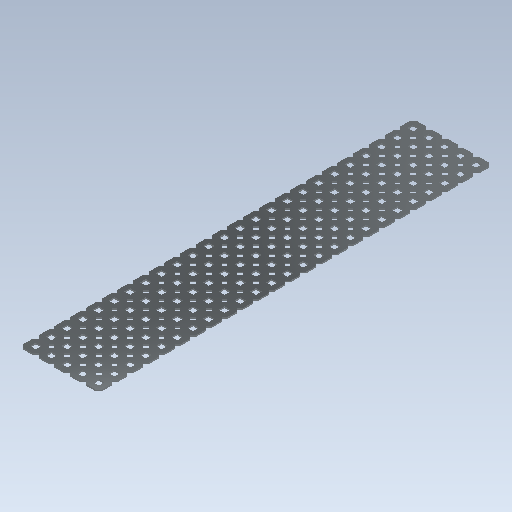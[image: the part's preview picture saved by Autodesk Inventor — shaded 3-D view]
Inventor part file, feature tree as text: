
AUTODESK INVENTOR PART (.ipt)
format: ipt  version: 2020 (Build 240168000, 168)  size: 2,339,840 bytes
history: native  units: mm (DEFAULTED — no unit token found)
features: other x125, extrude x125, imported_body x1, pattern_linear x1, sketch x1
ambient origin geometry x8: Origin, YZ Plane, XZ Plane, XY Plane, X Axis, Y Axis, Z Axis, Center Point
bodies: Solid1 (feature_tree)
feature tree (253):
  imported_body  "Base1"
  pattern_linear  "Rectangular Pattern1"  Spacing1=0.0mm  [1 undecoded]
  sketch  "Sketch1"  dims[d1=1.1684mm d2=0.0mm d3=250.0mm d5=12.7mm d6=50.0mm d8=12.7mm d9=0.0mm d10=0.0mm d11=0.0mm d12=0.0mm d13=0.0mm d14=0.0mm d15=0.0mm d16=0.0mm d17=0.0mm d18=0.0mm d19=0.0mm d20=0.0mm d21=0.0mm d22=0.0mm d23=0.0mm d24=0.0mm d25=0.0mm d26=0.0mm d27=0.0mm d28=0.0mm d29=0.0mm d30=0.0mm d31=0.0mm d32=0.0mm d33=0.0mm d34=0.0mm d35=0.0mm d36=0.0mm d37=0.0mm d38=0.0mm d39=0.0mm d40=0.0mm d41=0.0mm d42=0.0mm d43=0.0mm d44=0.0mm d45=0.0mm d46=0.0mm d47=0.0mm d48=0.0mm d49=0.0mm d50=0.0mm d51=0.0mm d52=0.0mm d53=0.0mm d54=0.0mm d55=0.0mm d56=0.0mm d57=0.0mm d58=0.0mm d59=0.0mm d60=0.0mm d61=0.0mm d62=0.0mm d63=0.0mm d64=0.0mm d65=0.0mm d66=0.0mm d67=0.0mm d68=0.0mm d69=0.0mm d70=0.0mm d71=0.0mm d72=0.0mm d73=0.0mm d74=0.0mm d75=0.0mm d76=0.0mm d77=0.0mm d78=0.0mm d79=0.0mm d80=0.0mm d81=0.0mm d82=0.0mm d83=0.0mm d84=0.0mm d85=0.0mm d86=0.0mm d87=0.0mm d88=0.0mm d89=0.0mm d90=0.0mm d91=0.0mm d92=0.0mm d93=0.0mm d94=0.0mm d95=0.0mm d96=0.0mm d97=0.0mm d98=0.0mm d99=0.0mm d100=0.0mm d101=0.0mm d102=0.0mm d103=0.0mm d104=0.0mm d105=0.0mm d106=0.0mm d107=0.0mm d108=0.0mm d109=0.0mm d110=0.0mm d111=0.0mm d112=0.0mm d113=0.0mm d114=0.0mm d115=0.0mm d116=0.0mm d117=0.0mm d118=0.0mm d119=0.0mm d120=0.0mm d121=0.0mm d122=0.0mm d123=0.0mm d124=0.0mm d125=0.0mm d126=0.0mm d127=0.0mm d128=0.0mm d129=0.0mm d130=0.0mm d131=0.0mm d132=0.0mm d133=0.0mm d134=0.0mm d135=0.0mm d136=0.0mm d137=0.0mm d138=0.0mm d139=0.0mm d140=0.0mm d141=0.0mm d142=0.0mm d143=0.0mm d144=0.0mm d145=0.0mm d146=0.0mm d147=0.0mm d148=0.0mm d149=0.0mm d150=0.0mm d151=0.0mm d152=0.0mm d153=0.0mm d154=0.0mm d155=0.0mm d156=0.0mm d157=0.0mm d158=0.0mm d159=0.0mm d160=0.0mm d161=0.0mm d162=0.0mm d163=0.0mm d164=0.0mm d165=0.0mm d166=0.0mm d167=0.0mm d168=0.0mm d169=0.0mm d170=0.0mm d171=0.0mm d172=0.0mm d173=0.0mm d174=0.0mm d175=0.0mm d176=0.0mm d177=0.0mm d178=0.0mm d179=0.0mm d180=0.0mm d181=0.0mm d182=0.0mm d183=0.0mm d184=0.0mm d185=0.0mm d186=0.0mm d187=0.0mm d188=0.0mm d189=0.0mm d190=0.0mm d191=0.0mm d192=0.0mm d193=0.0mm d194=0.0mm d195=0.0mm d196=0.0mm d197=0.0mm d198=0.0mm d199=0.0mm d200=0.0mm d201=0.0mm d202=0.0mm d203=0.0mm d204=0.0mm d205=0.0mm d206=0.0mm d207=0.0mm d208=0.0mm d209=0.0mm d210=0.0mm d211=0.0mm d212=0.0mm d213=0.0mm d214=0.0mm d215=0.0mm d216=0.0mm d217=0.0mm d218=0.0mm d219=0.0mm d220=0.0mm d221=0.0mm d222=0.0mm d223=0.0mm d224=0.0mm d225=0.0mm d226=0.0mm d227=0.0mm d228=0.0mm d229=0.0mm d230=0.0mm d231=0.0mm d232=0.0mm d233=0.0mm d234=0.0mm d235=0.0mm d236=0.0mm d237=0.0mm d238=0.0mm d239=0.0mm d240=0.0mm d241=0.0mm d242=0.0mm d243=0.0mm d244=0.0mm d245=0.0mm d246=0.0mm d247=0.0mm d248=0.0mm d249=0.0mm d250=0.0mm d251=0.0mm d252=0.0mm d253=0.0mm d254=0.0mm d255=0.0mm d256=0.0mm d257=0.0mm d258=0.0mm]
  other  "Srf1"
  other  "Srf2"
  other  "Srf3"
  other  "Srf4"
  other  "Srf5"
  other  "Srf6"
  other  "Srf7"
  other  "Srf8"
  other  "Srf9"
  other  "Srf10"
  other  "Srf11"
  other  "Srf12"
  other  "Srf13"
  other  "Srf14"
  other  "Srf15"
  other  "Srf16"
  other  "Srf17"
  other  "Srf18"
  other  "Srf19"
  other  "Srf20"
  other  "Srf21"
  other  "Srf22"
  other  "Srf23"
  other  "Srf24"
  other  "Srf25"
  other  "Srf26"
  other  "Srf27"
  other  "Srf28"
  other  "Srf29"
  other  "Srf30"
  other  "Srf31"
  other  "Srf32"
  other  "Srf33"
  other  "Srf34"
  other  "Srf35"
  other  "Srf36"
  other  "Srf37"
  other  "Srf38"
  other  "Srf39"
  other  "Srf40"
  other  "Srf41"
  other  "Srf42"
  other  "Srf43"
  other  "Srf44"
  other  "Srf45"
  other  "Srf46"
  other  "Srf47"
  other  "Srf48"
  other  "Srf49"
  other  "Srf50"
  other  "Srf51"
  other  "Srf52"
  other  "Srf53"
  other  "Srf54"
  other  "Srf55"
  other  "Srf56"
  other  "Srf57"
  other  "Srf58"
  other  "Srf59"
  other  "Srf60"
  other  "Srf61"
  other  "Srf62"
  other  "Srf63"
  other  "Srf64"
  other  "Srf65"
  other  "Srf66"
  other  "Srf67"
  other  "Srf68"
  other  "Srf69"
  other  "Srf70"
  other  "Srf71"
  other  "Srf72"
  other  "Srf73"
  other  "Srf74"
  other  "Srf75"
  other  "Srf76"
  other  "Srf77"
  other  "Srf78"
  other  "Srf79"
  other  "Srf80"
  other  "Srf81"
  other  "Srf82"
  other  "Srf83"
  other  "Srf84"
  other  "Srf85"
  other  "Srf86"
  other  "Srf87"
  other  "Srf88"
  other  "Srf89"
  other  "Srf90"
  other  "Srf91"
  other  "Srf92"
  other  "Srf93"
  other  "Srf94"
  other  "Srf95"
  other  "Srf96"
  other  "Srf97"
  other  "Srf98"
  other  "Srf99"
  other  "Srf100"
  other  "Srf101"
  other  "Srf102"
  other  "Srf103"
  other  "Srf104"
  other  "Srf105"
  other  "Srf106"
  other  "Srf107"
  other  "Srf108"
  other  "Srf109"
  other  "Srf110"
  other  "Srf111"
  other  "Srf112"
  other  "Srf113"
  other  "Srf114"
  other  "Srf115"
  other  "Srf116"
  other  "Srf117"
  other  "Srf118"
  other  "Srf119"
  other  "Srf120"
  other  "Srf121"
  other  "Srf122"
  other  "Srf123"
  other  "Srf124"
  other  "Srf125"
  extrude  "ExtrusionSrf1"  Depth=250.0mm
  extrude  "ExtrusionSrf2"  Depth=12.7mm
  extrude  "ExtrusionSrf3"  Depth=50.0mm
  extrude  "ExtrusionSrf4"  TaperAngle=0.0deg  [1 undecoded]
  extrude  "ExtrusionSrf5"  TaperAngle=0.0deg  [1 undecoded]
  extrude  "ExtrusionSrf6"  TaperAngle=0.0deg  [1 undecoded]
  extrude  "ExtrusionSrf7"  TaperAngle=0.0deg  [1 undecoded]
  extrude  "ExtrusionSrf8"  TaperAngle=0.0deg  [1 undecoded]
  extrude  "ExtrusionSrf9"  TaperAngle=0.0deg  [1 undecoded]
  extrude  "ExtrusionSrf10"  TaperAngle=0.0deg  [1 undecoded]
  extrude  "ExtrusionSrf11"  TaperAngle=0.0deg  [1 undecoded]
  extrude  "ExtrusionSrf12"  TaperAngle=0.0deg  [1 undecoded]
  extrude  "ExtrusionSrf13"  TaperAngle=0.0deg  [1 undecoded]
  extrude  "ExtrusionSrf14"  TaperAngle=0.0deg  [1 undecoded]
  extrude  "ExtrusionSrf15"  TaperAngle=0.0deg  [1 undecoded]
  extrude  "ExtrusionSrf16"  TaperAngle=0.0deg  [1 undecoded]
  extrude  "ExtrusionSrf17"  TaperAngle=0.0deg  [1 undecoded]
  extrude  "ExtrusionSrf18"  TaperAngle=0.0deg  [1 undecoded]
  extrude  "ExtrusionSrf19"  TaperAngle=0.0deg  [1 undecoded]
  extrude  "ExtrusionSrf20"  TaperAngle=0.0deg  [1 undecoded]
  extrude  "ExtrusionSrf21"  TaperAngle=0.0deg  [1 undecoded]
  extrude  "ExtrusionSrf22"  TaperAngle=0.0deg  [1 undecoded]
  extrude  "ExtrusionSrf23"  TaperAngle=0.0deg  [1 undecoded]
  extrude  "ExtrusionSrf24"  TaperAngle=0.0deg  [1 undecoded]
  extrude  "ExtrusionSrf25"  TaperAngle=0.0deg  [1 undecoded]
  extrude  "ExtrusionSrf26"  TaperAngle=0.0deg  [1 undecoded]
  extrude  "ExtrusionSrf27"  TaperAngle=0.0deg  [1 undecoded]
  extrude  "ExtrusionSrf28"  TaperAngle=0.0deg  [1 undecoded]
  extrude  "ExtrusionSrf29"  TaperAngle=0.0deg  [1 undecoded]
  extrude  "ExtrusionSrf30"  TaperAngle=0.0deg  [1 undecoded]
  extrude  "ExtrusionSrf31"  TaperAngle=0.0deg  [1 undecoded]
  extrude  "ExtrusionSrf32"  TaperAngle=0.0deg  [1 undecoded]
  extrude  "ExtrusionSrf33"  TaperAngle=0.0deg  [1 undecoded]
  extrude  "ExtrusionSrf34"  TaperAngle=0.0deg  [1 undecoded]
  extrude  "ExtrusionSrf35"  TaperAngle=0.0deg  [1 undecoded]
  extrude  "ExtrusionSrf36"  TaperAngle=0.0deg  [1 undecoded]
  extrude  "ExtrusionSrf37"  TaperAngle=0.0deg  [1 undecoded]
  extrude  "ExtrusionSrf38"  TaperAngle=0.0deg  [1 undecoded]
  extrude  "ExtrusionSrf39"  TaperAngle=0.0deg  [1 undecoded]
  extrude  "ExtrusionSrf40"  TaperAngle=0.0deg  [1 undecoded]
  extrude  "ExtrusionSrf41"  TaperAngle=0.0deg  [1 undecoded]
  extrude  "ExtrusionSrf42"  TaperAngle=0.0deg  [1 undecoded]
  extrude  "ExtrusionSrf43"  TaperAngle=0.0deg  [1 undecoded]
  extrude  "ExtrusionSrf44"  TaperAngle=0.0deg  [1 undecoded]
  extrude  "ExtrusionSrf45"  TaperAngle=0.0deg  [1 undecoded]
  extrude  "ExtrusionSrf46"  TaperAngle=0.0deg  [1 undecoded]
  extrude  "ExtrusionSrf47"  TaperAngle=0.0deg  [1 undecoded]
  extrude  "ExtrusionSrf48"  TaperAngle=0.0deg  [1 undecoded]
  extrude  "ExtrusionSrf49"  TaperAngle=0.0deg  [1 undecoded]
  extrude  "ExtrusionSrf50"  TaperAngle=0.0deg  [1 undecoded]
  extrude  "ExtrusionSrf51"  TaperAngle=0.0deg  [1 undecoded]
  extrude  "ExtrusionSrf52"  TaperAngle=0.0deg  [1 undecoded]
  extrude  "ExtrusionSrf53"  TaperAngle=0.0deg  [1 undecoded]
  extrude  "ExtrusionSrf54"  TaperAngle=0.0deg  [1 undecoded]
  extrude  "ExtrusionSrf55"  TaperAngle=0.0deg  [1 undecoded]
  extrude  "ExtrusionSrf56"  TaperAngle=0.0deg  [1 undecoded]
  extrude  "ExtrusionSrf57"  TaperAngle=0.0deg  [1 undecoded]
  extrude  "ExtrusionSrf58"  TaperAngle=0.0deg  [1 undecoded]
  extrude  "ExtrusionSrf59"  TaperAngle=0.0deg  [1 undecoded]
  extrude  "ExtrusionSrf60"  TaperAngle=0.0deg  [1 undecoded]
  extrude  "ExtrusionSrf61"  TaperAngle=0.0deg  [1 undecoded]
  extrude  "ExtrusionSrf62"  TaperAngle=0.0deg  [1 undecoded]
  extrude  "ExtrusionSrf63"  TaperAngle=0.0deg  [1 undecoded]
  extrude  "ExtrusionSrf64"  TaperAngle=0.0deg  [1 undecoded]
  extrude  "ExtrusionSrf65"  TaperAngle=0.0deg  [1 undecoded]
  extrude  "ExtrusionSrf66"  TaperAngle=0.0deg  [1 undecoded]
  extrude  "ExtrusionSrf67"  TaperAngle=0.0deg  [1 undecoded]
  extrude  "ExtrusionSrf68"  TaperAngle=0.0deg  [1 undecoded]
  extrude  "ExtrusionSrf69"  TaperAngle=0.0deg  [1 undecoded]
  extrude  "ExtrusionSrf70"  TaperAngle=0.0deg  [1 undecoded]
  extrude  "ExtrusionSrf71"  TaperAngle=0.0deg  [1 undecoded]
  extrude  "ExtrusionSrf72"  TaperAngle=0.0deg  [1 undecoded]
  extrude  "ExtrusionSrf73"  TaperAngle=0.0deg  [1 undecoded]
  extrude  "ExtrusionSrf74"  TaperAngle=0.0deg  [1 undecoded]
  extrude  "ExtrusionSrf75"  TaperAngle=0.0deg  [1 undecoded]
  extrude  "ExtrusionSrf76"  TaperAngle=0.0deg  [1 undecoded]
  extrude  "ExtrusionSrf77"  TaperAngle=0.0deg  [1 undecoded]
  extrude  "ExtrusionSrf78"  TaperAngle=0.0deg  [1 undecoded]
  extrude  "ExtrusionSrf79"  TaperAngle=0.0deg  [1 undecoded]
  extrude  "ExtrusionSrf80"  TaperAngle=0.0deg  [1 undecoded]
  extrude  "ExtrusionSrf81"  TaperAngle=0.0deg  [1 undecoded]
  extrude  "ExtrusionSrf82"  TaperAngle=0.0deg  [1 undecoded]
  extrude  "ExtrusionSrf83"  TaperAngle=0.0deg  [1 undecoded]
  extrude  "ExtrusionSrf84"  TaperAngle=0.0deg  [1 undecoded]
  extrude  "ExtrusionSrf85"  TaperAngle=0.0deg  [1 undecoded]
  extrude  "ExtrusionSrf86"  TaperAngle=0.0deg  [1 undecoded]
  extrude  "ExtrusionSrf87"  TaperAngle=0.0deg  [1 undecoded]
  extrude  "ExtrusionSrf88"  TaperAngle=0.0deg  [1 undecoded]
  extrude  "ExtrusionSrf89"  TaperAngle=0.0deg  [1 undecoded]
  extrude  "ExtrusionSrf90"  TaperAngle=0.0deg  [1 undecoded]
  extrude  "ExtrusionSrf91"  TaperAngle=0.0deg  [1 undecoded]
  extrude  "ExtrusionSrf92"  TaperAngle=0.0deg  [1 undecoded]
  extrude  "ExtrusionSrf93"  TaperAngle=0.0deg  [1 undecoded]
  extrude  "ExtrusionSrf94"  TaperAngle=0.0deg  [1 undecoded]
  extrude  "ExtrusionSrf95"  TaperAngle=0.0deg  [1 undecoded]
  extrude  "ExtrusionSrf96"  TaperAngle=0.0deg  [1 undecoded]
  extrude  "ExtrusionSrf97"  TaperAngle=0.0deg  [1 undecoded]
  extrude  "ExtrusionSrf98"  TaperAngle=0.0deg  [1 undecoded]
  extrude  "ExtrusionSrf99"  TaperAngle=0.0deg  [1 undecoded]
  extrude  "ExtrusionSrf100"  TaperAngle=0.0deg  [1 undecoded]
  extrude  "ExtrusionSrf101"  TaperAngle=0.0deg  [1 undecoded]
  extrude  "ExtrusionSrf102"  TaperAngle=0.0deg  [1 undecoded]
  extrude  "ExtrusionSrf103"  TaperAngle=0.0deg  [1 undecoded]
  extrude  "ExtrusionSrf104"  TaperAngle=0.0deg  [1 undecoded]
  extrude  "ExtrusionSrf105"  TaperAngle=0.0deg  [1 undecoded]
  extrude  "ExtrusionSrf106"  TaperAngle=0.0deg  [1 undecoded]
  extrude  "ExtrusionSrf107"  TaperAngle=0.0deg  [1 undecoded]
  extrude  "ExtrusionSrf108"  TaperAngle=0.0deg  [1 undecoded]
  extrude  "ExtrusionSrf109"  TaperAngle=0.0deg  [1 undecoded]
  extrude  "ExtrusionSrf110"  TaperAngle=0.0deg  [1 undecoded]
  extrude  "ExtrusionSrf111"  TaperAngle=0.0deg  [1 undecoded]
  extrude  "ExtrusionSrf112"  TaperAngle=0.0deg  [1 undecoded]
  extrude  "ExtrusionSrf113"  TaperAngle=0.0deg  [1 undecoded]
  extrude  "ExtrusionSrf114"  TaperAngle=0.0deg  [1 undecoded]
  extrude  "ExtrusionSrf115"  TaperAngle=0.0deg  [1 undecoded]
  extrude  "ExtrusionSrf116"  TaperAngle=0.0deg  [1 undecoded]
  extrude  "ExtrusionSrf117"  TaperAngle=0.0deg  [1 undecoded]
  extrude  "ExtrusionSrf118"  TaperAngle=0.0deg  [1 undecoded]
  extrude  "ExtrusionSrf119"  TaperAngle=0.0deg  [1 undecoded]
  extrude  "ExtrusionSrf120"  TaperAngle=0.0deg  [1 undecoded]
  extrude  "ExtrusionSrf121"  TaperAngle=0.0deg  [1 undecoded]
  extrude  "ExtrusionSrf122"  TaperAngle=0.0deg  [1 undecoded]
  extrude  "ExtrusionSrf123"  TaperAngle=0.0deg  [1 undecoded]
  extrude  "ExtrusionSrf124"  TaperAngle=0.0deg  [1 undecoded]
  extrude  "ExtrusionSrf125"  TaperAngle=0.0deg  [1 undecoded]
note: 123 required parameter values undecoded (feature->parameter linkage not recoverable at this tier; creation-order binding heuristic only, values carry confidence <= 0.55)
